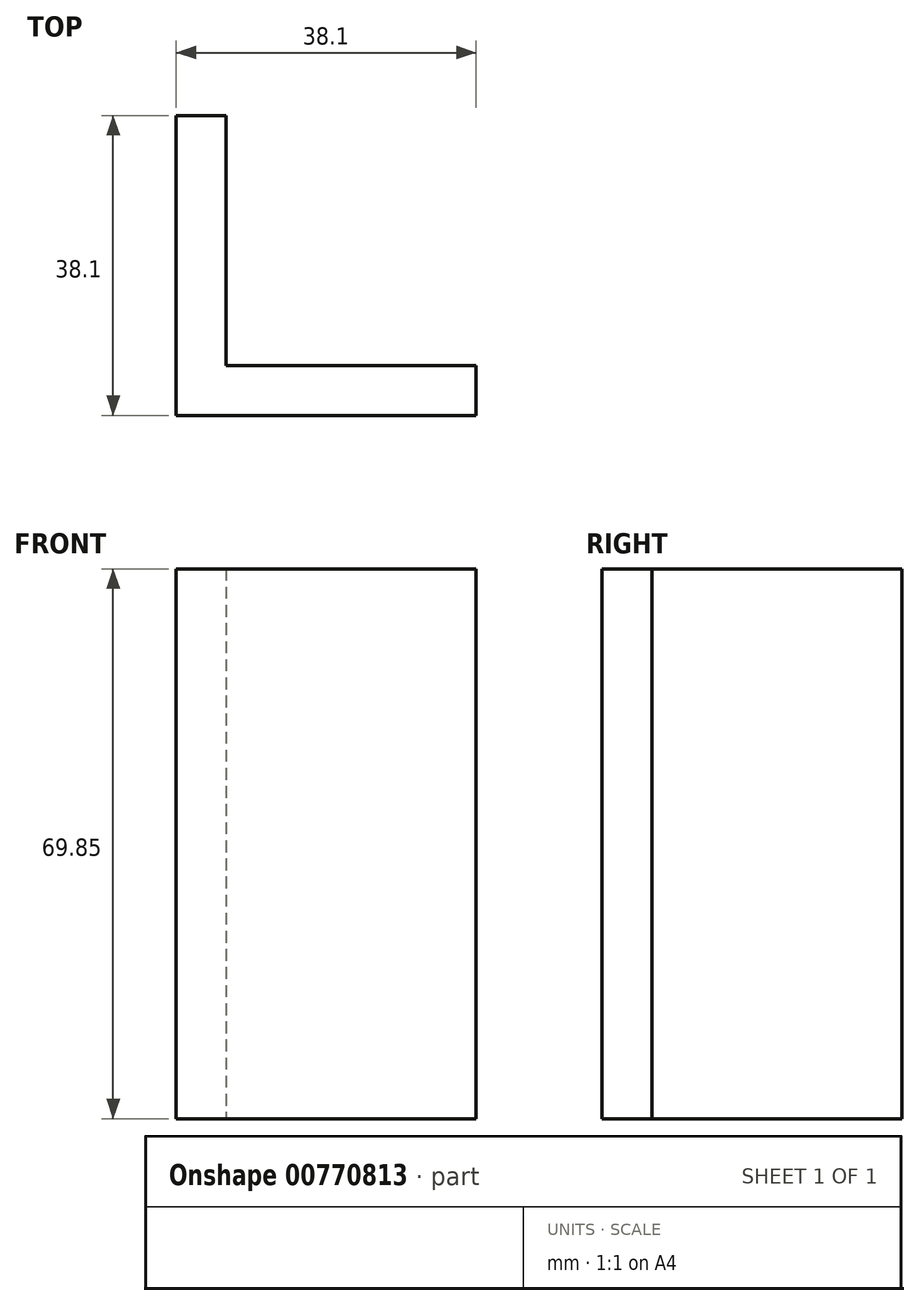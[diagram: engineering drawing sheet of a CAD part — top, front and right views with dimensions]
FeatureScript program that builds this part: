
annotation { "Feature Type Name" : "Feature", "Feature Type Description" : "" }
export const myFeature = defineFeature(function(context is Context, id is Id, definition is map)
    precondition{}
    {
        {
            var Q0;
            Q0=qCreatedBy(makeId("Top.planeOp"),FACE);
            var sketch = newSketch(context, id + "F0", { "sketchPlane" : qUnion([Q0])});
            skLineSegment(sketch, "E0", {"start": v(0, 0) * mm, "end": v(0, 38.1) * mm});
            skLineSegment(sketch, "E1", {"start": v(0, 38.1) * mm, "end": v(6.35, 38.1) * mm});
            skLineSegment(sketch, "E2", {"start": v(6.35, 38.1) * mm, "end": v(6.35, 6.35) * mm});
            skLineSegment(sketch, "E3", {"start": v(6.35, 6.35) * mm, "end": v(38.1, 6.35) * mm});
            skLineSegment(sketch, "E4", {"start": v(38.1, 6.35) * mm, "end": v(38.1, 0) * mm});
            skLineSegment(sketch, "E5", {"start": v(38.1, 0) * mm, "end": v(0, 0) * mm});
            skSolve(sketch);
        }
        {
            var Q0;
            Q0=makeQuery(id+"F0.imprint","IMPRINT",FACE,{"disambiguationData":[TD([[makeQuery(id+"F0.imprint","IMPRINT",EDGE,{"derivedFrom":sQuery(id+"F0.wireOp",EDGE,"E0")}),-1.0]])]});
            extrude(context, id + "F1", {"entities" : qUnion([Q0]), "depth" : 69.85 * mm, "offsetDistance" : 25.4 * mm});
        }
    });
